# Revit family: Access_Door-Heavy_Duty-Cendrex-Large_Openings-LHD
name_source: partatom
category: Specialty Equipment
revit_build: Autodesk Revit Architecture 2013 (Build: 20130531_2115(x64)
units: mm (PartAtom-declared; Revit-internal decimal feet)

## types (2) — shared parameters
Assembly Code = C1020700
Available Options = http://cendrex.com
Cendrex LEED Ready Program = http://www.cendrex.com
Construction Material = Metal - Cendrex - Aluminum
Default Elevation = 0"
Description = Heavy duty access door for large openings
Finish = Metal - Cendrex - Powder Coated White
Frame Depth = 2 1/2"
Manufacturer = Cendrex
Model = LHD
Product Documentation Link = http://cendrex.com
Product Page URL = http://cendrex.com
URL = http://www.cendrex.com

## per-type parameters (varying)
| type | Door Height | Door Height Calc | Door Width | Door Width Calc | Height Actual | Width Actual |
| 48 x 48 | 36" | 36" | 36" | 36" | 38 1/8" | 38 1/8" |
| Custom | 48" | 48" | 48" | 48" | 50 1/8" | 50 1/8" |

## geometry (parser evidence)
native form markers: Blend x22, Sweep x8
no freeform markers — native parametric forms only
